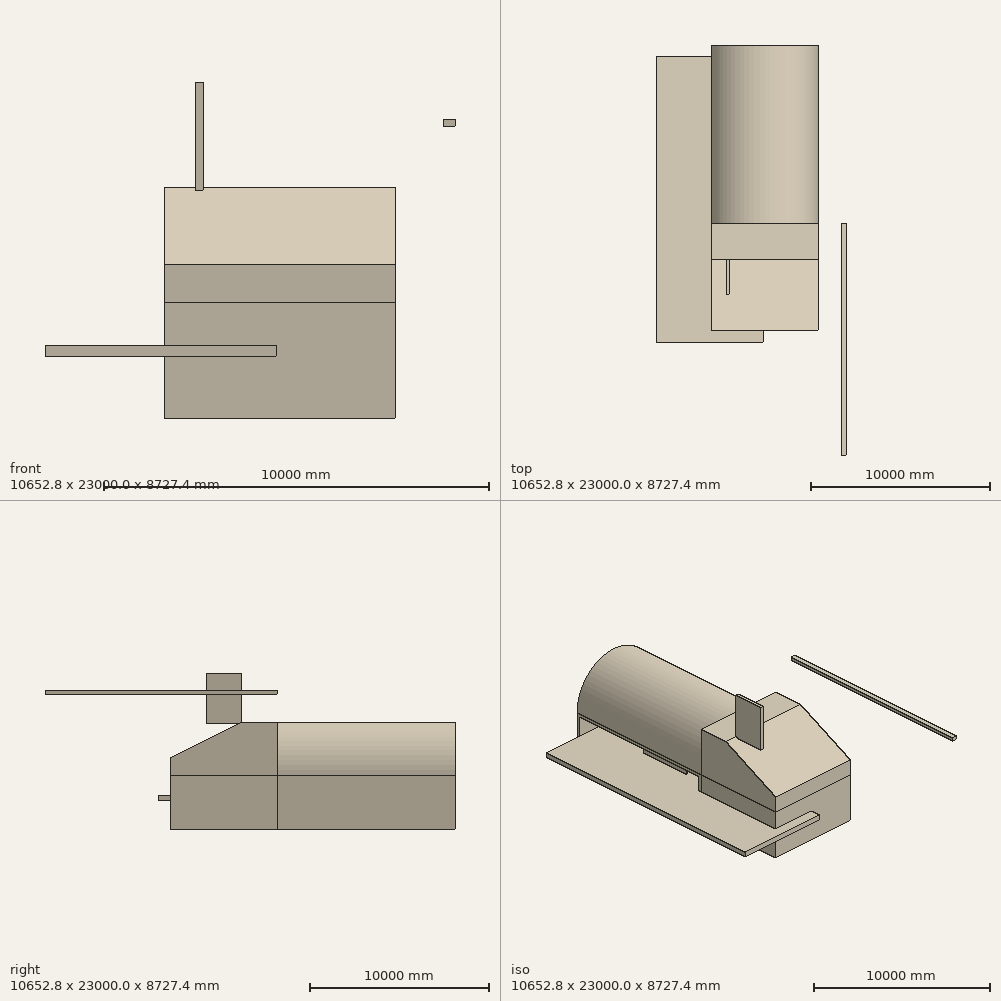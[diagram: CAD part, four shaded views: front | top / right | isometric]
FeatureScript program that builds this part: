
annotation { "Feature Type Name" : "Feature", "Feature Type Description" : "" }
export const myFeature = defineFeature(function(context is Context, id is Id, definition is map)
    precondition{}
    {
        {
            var Q0;
            Q0=qCreatedBy(makeId("Front.planeOp"),FACE);
            var sketch = newSketch(context, id + "F0", { "sketchPlane" : qUnion([Q0])});
            skLineSegment(sketch, "E0.bottom", {"start": v(-800.15, -1598.41) * mm, "end": v(5199.85, -1598.41) * mm});
            skLineSegment(sketch, "E0.top", {"start": v(-800.15, 1401.59) * mm, "end": v(5199.85, 1401.59) * mm});
            skLineSegment(sketch, "E0.left", {"start": v(-800.15, -1598.41) * mm, "end": v(-800.15, 1401.59) * mm});
            skLineSegment(sketch, "E0.right", {"start": v(5199.85, -1598.41) * mm, "end": v(5199.85, 1401.59) * mm});
            skArc(sketch, "E1", {"start": v(5199.85, 1401.59) * mm, "mid": v(2199.85, 4401.59) * mm, "end": v(-800.15, 1401.59) * mm});
            skLineSegment(sketch, "E2.bottom", {"start": v(6450.49, 6179.4) * mm, "end": v(6750.49, 6179.4) * mm});
            skLineSegment(sketch, "E2.top", {"start": v(6450.49, 5979.4) * mm, "end": v(6750.49, 5979.4) * mm});
            skLineSegment(sketch, "E2.left", {"start": v(6450.49, 6179.4) * mm, "end": v(6450.49, 5979.4) * mm});
            skLineSegment(sketch, "E2.right", {"start": v(6750.49, 6179.4) * mm, "end": v(6750.49, 5979.4) * mm});
            skSolve(sketch);
        }
        {
            var Q0;
            Q0=makeQuery(id+"F0.imprint","IMPRINT",FACE,{"disambiguationData":[TD([[makeQuery(id+"F0.imprint","IMPRINT",EDGE,{"derivedFrom":sQuery(id+"F0.wireOp",EDGE,"E0.bottom")}),1.0]])]});
            extrude(context, id + "F1", {"entities" : qUnion([Q0]), "depth" : 6000 * mm});
        }
        {
            var Q0;
            Q0=makeQuery(id+"F1.opExtrude","SWEPT_FACE",FACE,{"disambiguationData":[OSD([sQuery(id+"F0.wireOp",EDGE,"E0.top")])]});
            extrude(context, id + "F2", {"entities" : qUnion([Q0]), "depth" : 3000 * mm});
        }
        {
            var Q0;
            Q0=makeQuery(id+"F0.imprint","IMPRINT",FACE,{"disambiguationData":[TD([[makeQuery(id+"F0.imprint","IMPRINT",EDGE,{"derivedFrom":sQuery(id+"F0.wireOp",EDGE,"E0.bottom")}),1.0]])]});
            extrude(context, id + "F3", {"entities" : qUnion([Q0]), "oppositeDirection" : true, "depth" : 10000 * mm});
        }
        {
            var Q0;
            Q0=makeQuery(id+"F0.imprint","IMPRINT",FACE,{"disambiguationData":[TD([[makeQuery(id+"F0.imprint","IMPRINT",EDGE,{"derivedFrom":sQuery(id+"F0.wireOp",EDGE,"E0.top")}),1.0]])]});
            extrude(context, id + "F4", {"entities" : qUnion([Q0]), "oppositeDirection" : true, "depth" : 10000 * mm});
        }
        {
            var Q0;
            {var subQ0=sQuery(id+"F0.wireOp",EDGE,"E0.top");Q0=makeQuery(id+"F2.opExtrude","CAP_EDGE",EDGE,{"disambiguationData":[OSD([subQ0]),TDD([makeQuery(id+"F1.opExtrude","CAP_EDGE",EDGE,{"disambiguationData":[OSD([subQ0])],"isStart":false})])],"isStart":false});}
            chamfer(context, id + "F5", {"entities" : qUnion([Q0]), "chamferType" : ChamferType.TWO_OFFSETS, "width1" : 4000 * mm, "oppositeDirection" : false, "width2" : 2000 * mm, "tangentPropagation" : true});
        }
        {
            var Q0;
            Q0=makeQuery(id+"F3.opExtrude","SWEPT_FACE",FACE,{"disambiguationData":[OSD([sQuery(id+"F0.wireOp",EDGE,"E0.left")])]});
            var Q1;
            Q1=makeQuery(id+"F3.opExtrude","SWEPT_FACE",FACE,{"disambiguationData":[OSD([sQuery(id+"F0.wireOp",EDGE,"E0.bottom")])]});
            var Q2;
            Q2=makeQuery(id+"F3.opExtrude","SWEPT_BODY",BODY,{"disambiguationData":[OSD([sQuery(id+"F0.wireOp",EDGE,"E0.bottom"),sQuery(id+"F0.wireOp",EDGE,"E0.top"),sQuery(id+"F0.wireOp",EDGE,"E0.left"),sQuery(id+"F0.wireOp",EDGE,"E0.right")])]});
            shell(context, id + "F6", {"entities" : qUnion([Q0, Q1]), "parts" : qUnion([Q2]), "thickness" : 200 * mm});
        }
        {
            var Q0;
            Q0=qCreatedBy(makeId("Right.planeOp"),FACE);
            var sketch = newSketch(context, id + "F7", { "sketchPlane" : qUnion([Q0])});
            skLineSegment(sketch, "E3.bottom", {"start": v(5448.45, 2370.14) * mm, "end": v(1948.45, 2370.14) * mm});
            skLineSegment(sketch, "E3.top", {"start": v(5448.45, -629.86) * mm, "end": v(1948.45, -629.86) * mm});
            skLineSegment(sketch, "E3.left", {"start": v(5448.45, 2370.14) * mm, "end": v(5448.45, -629.86) * mm});
            skLineSegment(sketch, "E3.right", {"start": v(1948.45, 2370.14) * mm, "end": v(1948.45, -629.86) * mm});
            skLineSegment(sketch, "E4.bottom", {"start": v(-3994.9, 7128.95) * mm, "end": v(-1994.9, 7128.95) * mm});
            skLineSegment(sketch, "E4.top", {"start": v(-3994.9, 4328.95) * mm, "end": v(-1994.9, 4328.95) * mm});
            skLineSegment(sketch, "E4.left", {"start": v(-3994.9, 7128.95) * mm, "end": v(-3994.9, 4328.95) * mm});
            skLineSegment(sketch, "E4.right", {"start": v(-1994.9, 7128.95) * mm, "end": v(-1994.9, 4328.95) * mm});
            skSolve(sketch);
        }
        {
            var Q0;
            Q0=makeQuery(id+"F7.imprint","IMPRINT",FACE,{"disambiguationData":[TD([[makeQuery(id+"F7.imprint","IMPRINT",EDGE,{"derivedFrom":sQuery(id+"F7.wireOp",EDGE,"E3.bottom")}),1.0]])]});
            extrude(context, id + "F8", {"entities" : qUnion([Q0]), "depth" : 50 * mm});
        }
        {
            var Q0;
            Q0=makeQuery(id+"F0.imprint","IMPRINT",FACE,{"disambiguationData":[TD([[makeQuery(id+"F0.imprint","IMPRINT",EDGE,{"derivedFrom":sQuery(id+"F0.wireOp",EDGE,"E2.bottom")}),-1.0]])]});
            extrude(context, id + "F9", {"entities" : qUnion([Q0]), "depth" : 13000 * mm});
        }
        {
            var Q0;
            Q0=makeQuery(id+"F7.imprint","IMPRINT",FACE,{"disambiguationData":[TD([[makeQuery(id+"F7.imprint","IMPRINT",EDGE,{"derivedFrom":sQuery(id+"F7.wireOp",EDGE,"E4.bottom")}),-1.0]])]});
            extrude(context, id + "F10", {"entities" : qUnion([Q0]), "depth" : 200 * mm});
        }
        {
            var Q0;
            Q0=qCreatedBy(makeId("Top.planeOp"),FACE);
            var sketch = newSketch(context, id + "F11", { "sketchPlane" : qUnion([Q0])});
            skLineSegment(sketch, "E5.bottom", {"start": v(2097.72, 9356.9) * mm, "end": v(-3902.28, 9356.9) * mm});
            skLineSegment(sketch, "E5.top", {"start": v(2097.72, -6643.1) * mm, "end": v(-3902.28, -6643.1) * mm});
            skLineSegment(sketch, "E5.left", {"start": v(2097.72, 9356.9) * mm, "end": v(2097.72, -6643.1) * mm});
            skLineSegment(sketch, "E5.right", {"start": v(-3902.28, 9356.9) * mm, "end": v(-3902.28, -6643.1) * mm});
            skSolve(sketch);
        }
        {
            var Q0;
            Q0=makeQuery(id+"F11.imprint","IMPRINT",FACE,{"disambiguationData":[TD([[makeQuery(id+"F11.imprint","IMPRINT",EDGE,{"derivedFrom":sQuery(id+"F11.wireOp",EDGE,"E5.bottom")}),1.0]])]});
            extrude(context, id + "F12", {"entities" : qUnion([Q0]), "depth" : 300 * mm});
        }
    });
